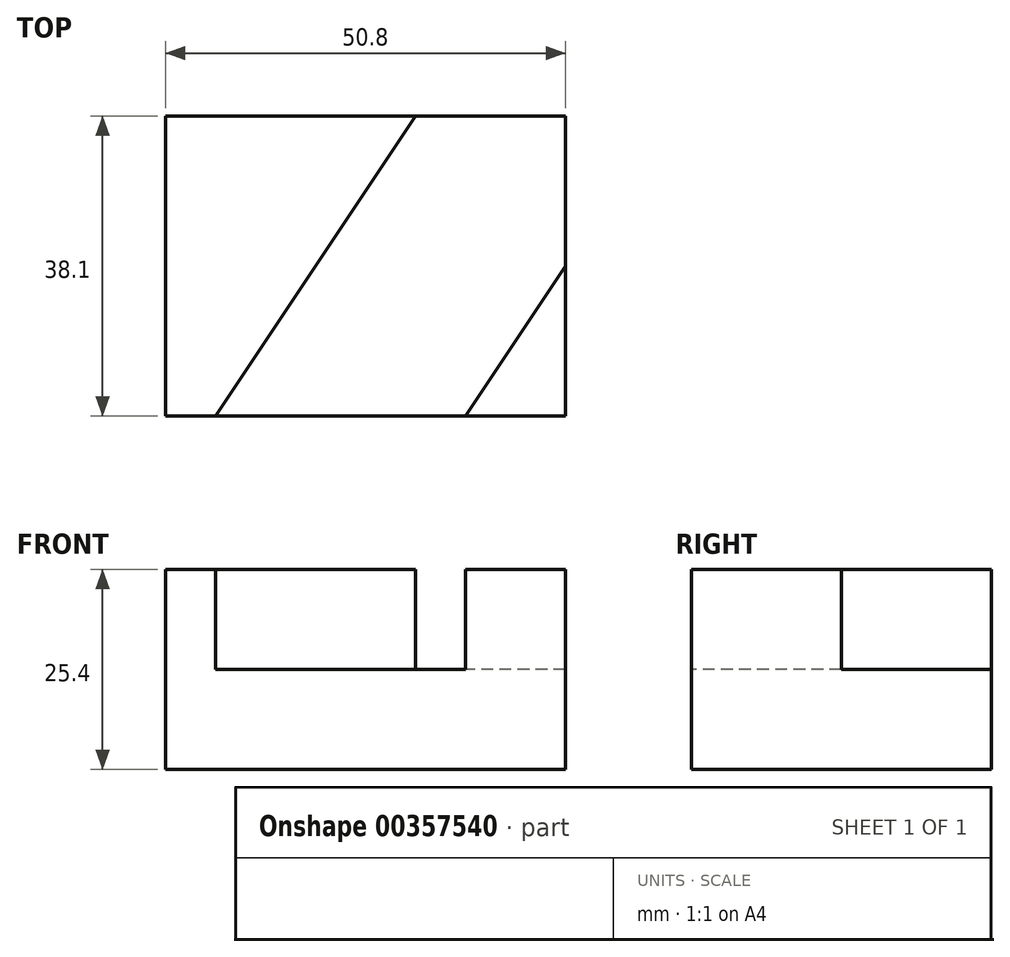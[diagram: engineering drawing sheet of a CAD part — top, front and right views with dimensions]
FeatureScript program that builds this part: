
annotation { "Feature Type Name" : "Feature", "Feature Type Description" : "" }
export const myFeature = defineFeature(function(context is Context, id is Id, definition is map)
    precondition{}
    {
        {
            var Q0;
            Q0=qCreatedBy(makeId("Top.planeOp"),FACE);
            var sketch = newSketch(context, id + "F0", { "sketchPlane" : qUnion([Q0])});
            skLineSegment(sketch, "E0", {"start": v(-28.61, 43.64) * mm, "end": v(-28.61, 5.54) * mm});
            skLineSegment(sketch, "E1", {"start": v(-28.61, 5.54) * mm, "end": v(22.19, 5.54) * mm});
            skLineSegment(sketch, "E2", {"start": v(22.19, 5.54) * mm, "end": v(22.19, 43.64) * mm});
            skLineSegment(sketch, "E3", {"start": v(22.19, 43.64) * mm, "end": v(-28.61, 43.64) * mm});
            skSolve(sketch);
        }
        {
            var Q0;
            Q0=makeQuery(id+"F0.imprint","IMPRINT",FACE,{"disambiguationData":[TD([[makeQuery(id+"F0.imprint","IMPRINT",EDGE,{"derivedFrom":sQuery(id+"F0.wireOp",EDGE,"E0")}),1.0]])]});
            extrude(context, id + "F1", {"entities" : qUnion([Q0]), "depth" : 12.7 * mm});
        }
        {
            var Q0;
            Q0=makeQuery(id+"F1.opExtrude","CAP_FACE",FACE,{"disambiguationData":[OSD([sQuery(id+"F0.wireOp",EDGE,"E0"),sQuery(id+"F0.wireOp",EDGE,"E1"),sQuery(id+"F0.wireOp",EDGE,"E2"),sQuery(id+"F0.wireOp",EDGE,"E3")])],"isStart":false});
            var sketch = newSketch(context, id + "F2", { "sketchPlane" : qUnion([Q0])});
            skLineSegment(sketch, "E4", {"start": v(3.14, 43.64) * mm, "end": v(-28.61, 43.64) * mm});
            skLineSegment(sketch, "E5", {"start": v(-28.61, 43.64) * mm, "end": v(-28.61, 5.54) * mm});
            skLineSegment(sketch, "E6", {"start": v(-28.61, 5.54) * mm, "end": v(-22.26, 5.54) * mm});
            skLineSegment(sketch, "E7", {"start": v(3.14, 43.64) * mm, "end": v(-22.26, 5.54) * mm});
            skSolve(sketch);
        }
        {
            var Q0;
            Q0=makeQuery(id+"F2.imprint","IMPRINT",FACE,{"disambiguationData":[TD([[makeQuery(id+"F2.imprint","IMPRINT",EDGE,{"derivedFrom":sQuery(id+"F2.wireOp",EDGE,"E4")}),1.0]])]});
            extrude(context, id + "F3", {"entities" : qUnion([Q0]), "operationType" : NewBodyOperationType.ADD, "depth" : 12.7 * mm});
        }
        {
            var Q0;
            Q0=makeQuery(id+"F1.opExtrude","CAP_FACE",FACE,{"disambiguationData":[OSD([sQuery(id+"F0.wireOp",EDGE,"E0"),sQuery(id+"F0.wireOp",EDGE,"E1"),sQuery(id+"F0.wireOp",EDGE,"E2"),sQuery(id+"F0.wireOp",EDGE,"E3")])],"isStart":false});
            var sketch = newSketch(context, id + "F4", { "sketchPlane" : qUnion([Q0])});
            skLineSegment(sketch, "E8", {"start": v(22.19, 24.59) * mm, "end": v(22.19, 5.54) * mm});
            skLineSegment(sketch, "E9", {"start": v(22.19, 5.54) * mm, "end": v(9.49, 5.54) * mm});
            skLineSegment(sketch, "E10", {"start": v(22.19, 24.59) * mm, "end": v(9.49, 5.54) * mm});
            skSolve(sketch);
        }
        {
            var Q0;
            Q0 = qSketchRegion(id + "F4", true);
            extrude(context, id + "F5", {"entities" : qUnion([Q0]), "operationType" : NewBodyOperationType.ADD, "depth" : 12.7 * mm});
        }
    });
